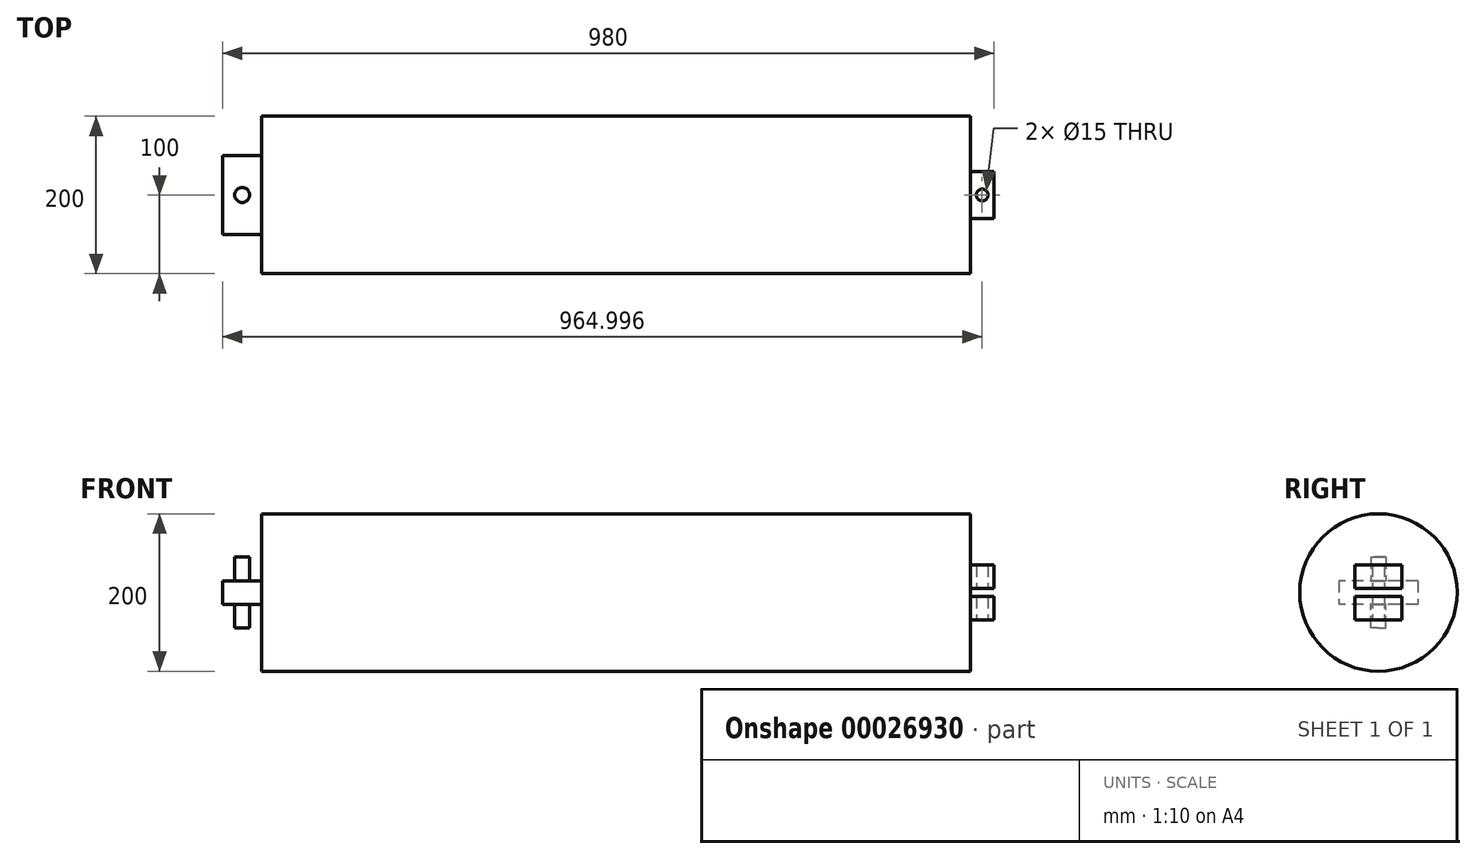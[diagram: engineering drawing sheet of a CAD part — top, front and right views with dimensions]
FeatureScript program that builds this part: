
annotation { "Feature Type Name" : "Feature", "Feature Type Description" : "" }
export const myFeature = defineFeature(function(context is Context, id is Id, definition is map)
    precondition{}
    {
        {
            var Q0;
            Q0=qCreatedBy(makeId("Front.planeOp"),FACE);
            var sketch = newSketch(context, id + "F0", { "sketchPlane" : qUnion([Q0])});
            skLineSegment(sketch, "E0.bottom", {"start": v(-394.93, -30.98) * mm, "end": v(505.07, -30.98) * mm});
            skLineSegment(sketch, "E0.top", {"start": v(-394.93, -130.98) * mm, "end": v(505.07, -130.98) * mm});
            skLineSegment(sketch, "E1", {"start": v(-394.93, -130.98) * mm, "end": v(-394.93, -30.98) * mm});
            skLineSegment(sketch, "E2", {"start": v(505.07, -30.98) * mm, "end": v(505.07, -130.98) * mm});
            skSolve(sketch);
        }
        {
            var Q0;
            {var subQ2=sQuery(id+"F0.wireOp",EDGE,"E0.bottom");Q0=makeQuery(id+"F0.imprint","IMPRINT",FACE,{"disambiguationData":[TD([[makeQuery(id+"F0.imprint","IMPRINT",EDGE,{"derivedFrom":subQ2}),-1.0]])]});}
            var Q1;
            Q1=sQuery(id+"F0.wireOp",EDGE,"E0.top");
            revolve(context, id + "F1", {"entities" : qUnion([Q0]), "axis" : qUnion([Q1]), "revolveType" : RevolveType.FULL});
        }
        {
            var Q0;
            Q0=makeQuery(id+"F1.opRevolve","SWEPT_FACE",FACE,{"disambiguationData":[OSD([sQuery(id+"F0.wireOp",EDGE,"E1")])]});
            var sketch = newSketch(context, id + "F2", { "sketchPlane" : qUnion([Q0])});
            skLineSegment(sketch, "E3.bottom", {"start": v(-50, -115.98) * mm, "end": v(50, -115.98) * mm});
            skLineSegment(sketch, "E3.top", {"start": v(-50, -145.98) * mm, "end": v(50, -145.98) * mm});
            skLineSegment(sketch, "E3.left", {"start": v(-50, -115.98) * mm, "end": v(-50, -145.98) * mm});
            skLineSegment(sketch, "E3.right", {"start": v(50, -115.98) * mm, "end": v(50, -145.98) * mm});
            skSolve(sketch);
        }
        {
            var Q0;
            Q0=makeQuery(id+"F2.imprint","IMPRINT",FACE,{"disambiguationData":[TD([[makeQuery(id+"F2.imprint","IMPRINT",EDGE,{"derivedFrom":sQuery(id+"F2.wireOp",EDGE,"E3.bottom")}),-1.0]])]});
            extrude(context, id + "F3", {"entities" : qUnion([Q0]), "operationType" : NewBodyOperationType.ADD, "depth" : 50 * mm});
        }
        {
            var Q0;
            Q0=makeQuery(id+"F3.opExtrude","SWEPT_FACE",FACE,{"disambiguationData":[OSD([sQuery(id+"F2.wireOp",EDGE,"E3.top")])]});
            var sketch = newSketch(context, id + "F4", { "sketchPlane" : qUnion([Q0])});
            skCircle(sketch, "E4", {"center": v(-419.93, 0) * mm, "radius": 9.5 * mm});
            skSolve(sketch);
        }
        {
            var Q0;
            Q0=makeQuery(id+"F3.opExtrude","SWEPT_FACE",FACE,{"disambiguationData":[OSD([sQuery(id+"F2.wireOp",EDGE,"E3.bottom")])]});
            var sketch = newSketch(context, id + "F5", { "sketchPlane" : qUnion([Q0])});
            skCircle(sketch, "E5", {"center": v(-419.93, 0) * mm, "radius": 9.5 * mm});
            skSolve(sketch);
        }
        {
            var Q0;
            Q0=makeQuery(id+"F4.imprint","IMPRINT",FACE,{"disambiguationData":[TD([[makeQuery(id+"F4.imprint","IMPRINT",EDGE,{"derivedFrom":sQuery(id+"F4.wireOp",EDGE,"E4")}),1.0]])]});
            extrude(context, id + "F6", {"entities" : qUnion([Q0]), "operationType" : NewBodyOperationType.ADD, "depth" : 30 * mm});
        }
        {
            var Q0;
            Q0=makeQuery(id+"F5.imprint","IMPRINT",FACE,{"disambiguationData":[TD([[makeQuery(id+"F5.imprint","IMPRINT",EDGE,{"derivedFrom":sQuery(id+"F5.wireOp",EDGE,"E5")}),1.0]])]});
            extrude(context, id + "F7", {"entities" : qUnion([Q0]), "operationType" : NewBodyOperationType.ADD, "depth" : 30 * mm});
        }
        {
            var Q0;
            Q0=makeQuery(id+"F1.opRevolve","SWEPT_FACE",FACE,{"disambiguationData":[OSD([sQuery(id+"F0.wireOp",EDGE,"E2")])]});
            var sketch = newSketch(context, id + "F8", { "sketchPlane" : qUnion([Q0])});
            skLineSegment(sketch, "E6", {"start": v(30, -125.98) * mm, "end": v(-30, -125.98) * mm});
            skLineSegment(sketch, "E7", {"start": v(-30, -135.98) * mm, "end": v(30, -135.98) * mm});
            skLineSegment(sketch, "E8", {"start": v(-30, -125.98) * mm, "end": v(-30, -95.98) * mm});
            skLineSegment(sketch, "E9", {"start": v(-30, -135.98) * mm, "end": v(-30, -165.98) * mm});
            skLineSegment(sketch, "E10", {"start": v(30, -135.98) * mm, "end": v(30, -165.98) * mm});
            skLineSegment(sketch, "E11", {"start": v(30, -165.98) * mm, "end": v(-30, -165.98) * mm});
            skLineSegment(sketch, "E12", {"start": v(30, -125.98) * mm, "end": v(30, -95.98) * mm});
            skLineSegment(sketch, "E13", {"start": v(-30, -95.98) * mm, "end": v(30, -95.98) * mm});
            skSolve(sketch);
        }
        {
            var Q0;
            Q0=makeQuery(id+"F8.imprint","IMPRINT",FACE,{"disambiguationData":[TD([[makeQuery(id+"F8.imprint","IMPRINT",EDGE,{"derivedFrom":sQuery(id+"F8.wireOp",EDGE,"E6")}),-1.0]])]});
            extrude(context, id + "F9", {"entities" : qUnion([Q0]), "operationType" : NewBodyOperationType.ADD, "depth" : 30 * mm});
        }
        {
            var Q0;
            Q0=makeQuery(id+"F8.imprint","IMPRINT",FACE,{"disambiguationData":[TD([[makeQuery(id+"F8.imprint","IMPRINT",EDGE,{"derivedFrom":sQuery(id+"F8.wireOp",EDGE,"E7")}),-1.0]])]});
            extrude(context, id + "F10", {"entities" : qUnion([Q0]), "operationType" : NewBodyOperationType.ADD, "depth" : 30 * mm});
        }
        {
            var Q0;
            Q0=makeQuery(id+"F10.opExtrude","SWEPT_FACE",FACE,{"disambiguationData":[OSD([sQuery(id+"F8.wireOp",EDGE,"E11")])]});
            var sketch = newSketch(context, id + "F11", { "sketchPlane" : qUnion([Q0])});
            skCircle(sketch, "E14", {"center": v(520.07, 0) * mm, "radius": 7.5 * mm});
            skSolve(sketch);
        }
        {
            var Q0;
            Q0=makeQuery(id+"F11.imprint","IMPRINT",FACE,{"disambiguationData":[TD([[makeQuery(id+"F11.imprint","IMPRINT",EDGE,{"derivedFrom":sQuery(id+"F11.wireOp",EDGE,"E14")}),1.0]])]});
            extrude(context, id + "F12", {"entities" : qUnion([Q0]), "operationType" : NewBodyOperationType.REMOVE, "oppositeDirection" : true, "depth" : 70 * mm});
        }
    });
